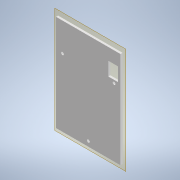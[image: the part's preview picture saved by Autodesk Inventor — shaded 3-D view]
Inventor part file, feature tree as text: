
AUTODESK INVENTOR PART (.ipt)
format: ipt  version: 2022 (Build 260153000, 153)  size: 136,192 bytes
history: native  units: mm
features: reference x11, other x5, extrude x2, sketch x2
ambient origin geometry x8: Origin, YZ Plane, XZ Plane, XY Plane, X Axis, Y Axis, Z Axis, Center Point
bodies: Body1 (feature_tree)
feature tree (20):
  other  "Твердое тело1"
  other  "РабПлоскость1"
  extrude  "Выдавливание1"  Depth=4.0mm
  extrude  "Выдавливание2"  Depth=4.0mm
  sketch  "Эскиз1"
  reference  "Ссылка1"
  reference  "Ссылка2"
  reference  "Ссылка3"
  reference  "Ссылка4"
  reference  "Ссылка5"
  reference  "Ссылка6"
  reference  "Ссылка7"
  sketch  "Эскиз2"
  reference  "Ссылка8"
  reference  "Ссылка9"
  reference  "Ссылка10"
  reference  "Ссылка11"
  other  "Сборка2"
  other  "корпус:1"
  other  "goruntu modulu:1"
